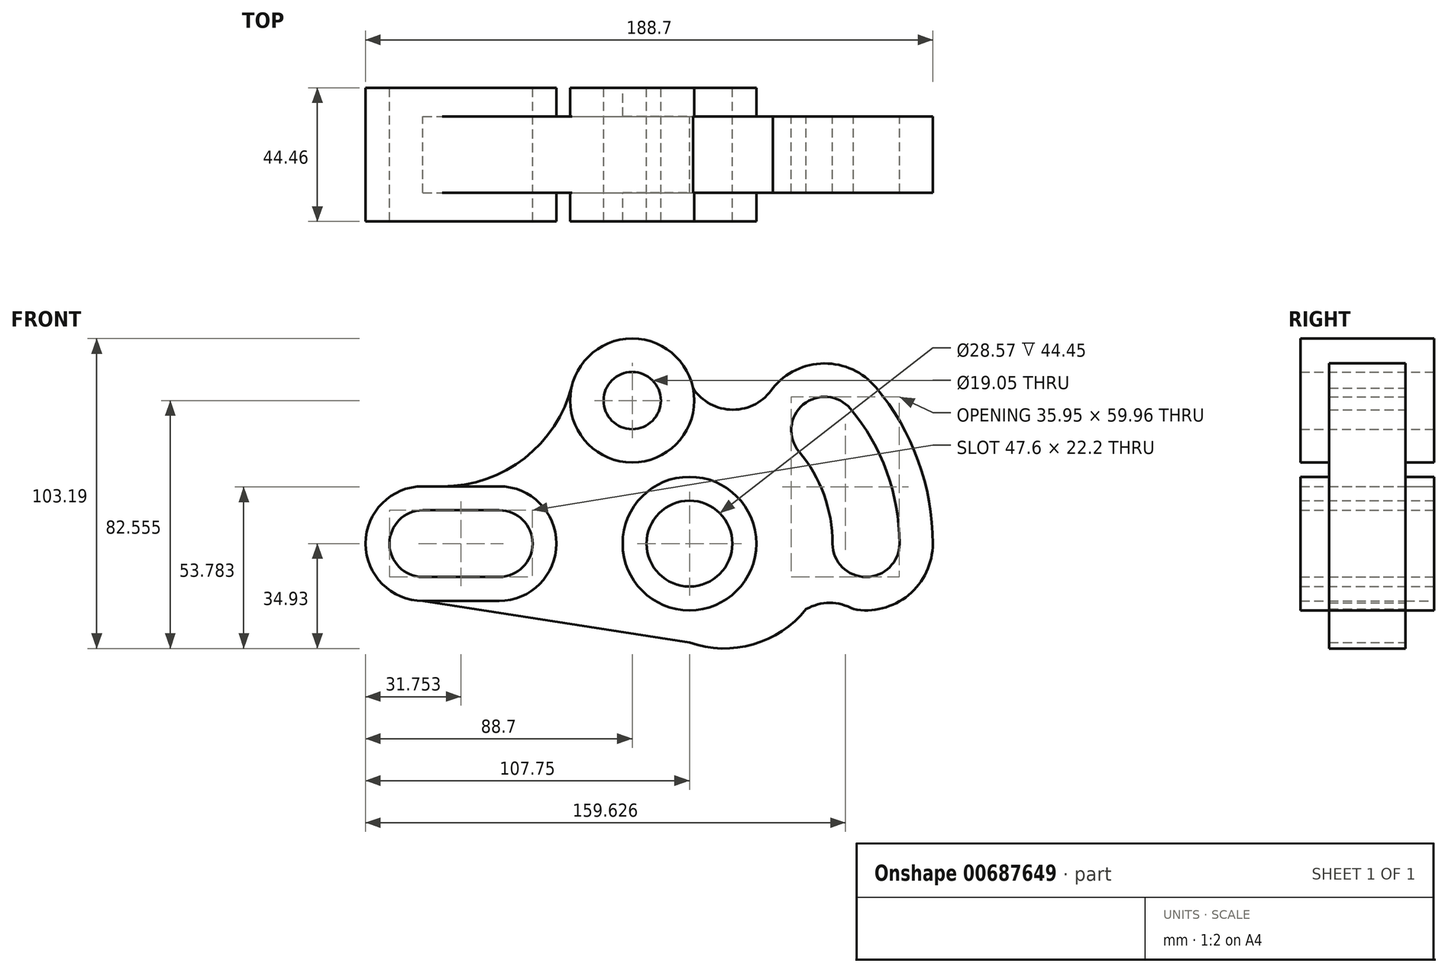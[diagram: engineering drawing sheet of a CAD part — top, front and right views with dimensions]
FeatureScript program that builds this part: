
annotation { "Feature Type Name" : "Feature", "Feature Type Description" : "" }
export const myFeature = defineFeature(function(context is Context, id is Id, definition is map)
    precondition{}
    {
        {
            var Q0;
            Q0=qCreatedBy(makeId("Front.planeOp"),FACE);
            var sketch = newSketch(context, id + "F0", { "sketchPlane" : qUnion([Q0])});
            skCircle(sketch, "E0", {"center": v(0, 0) * mm, "radius": 14.29 * mm});
            skCircle(sketch, "E1", {"center": v(0, 0) * mm, "radius": 22.23 * mm});
            skLineSegment(sketch, "E2", {"start": v(0, 0) * mm, "end": v(58.72, 0) * mm, "construction": true});
            skLineSegment(sketch, "E3", {"start": v(0, 0) * mm, "end": v(44.99, 37.75) * mm, "construction": true});
            skArc(sketch, "E4", {"start": v(44.99, 37.75) * mm, "mid": v(55.18, 20.09) * mm, "end": v(58.72, 0) * mm, "construction": true});
            skArc(sketch, "E5", {"start": v(36.46, 30.6) * mm, "mid": v(37.83, 46.27) * mm, "end": v(53.5, 44.9) * mm});
            skArc(sketch, "E6", {"start": v(47.6, 0) * mm, "mid": v(58.72, -11.13) * mm, "end": v(69.85, 0) * mm});
            skArc(sketch, "E7", {"start": v(53.5, 44.9) * mm, "mid": v(65.64, 23.9) * mm, "end": v(69.85, 0) * mm});
            skArc(sketch, "E8", {"start": v(36.46, 30.6) * mm, "mid": v(44.73, 16.28) * mm, "end": v(47.6, 0) * mm});
            skArc(sketch, "E9", {"start": v(-88.7, 11.1) * mm, "mid": v(-99.8, 0) * mm, "end": v(-88.7, -11.1) * mm});
            skArc(sketch, "E10", {"start": v(-63.3, 11.1) * mm, "mid": v(-52.2, 0) * mm, "end": v(-63.3, -11.1) * mm});
            skLineSegment(sketch, "E11", {"start": v(-88.7, 11.1) * mm, "end": v(-63.3, 11.1) * mm});
            skLineSegment(sketch, "E12", {"start": v(-88.7, -11.1) * mm, "end": v(-63.3, -11.1) * mm});
            skArc(sketch, "E13", {"start": v(-88.7, 19.05) * mm, "mid": v(-107.75, 0) * mm, "end": v(-88.7, -19.05) * mm});
            skLineSegment(sketch, "E14", {"start": v(-88.7, 19.05) * mm, "end": v(-63.3, 19.05) * mm});
            skLineSegment(sketch, "E15", {"start": v(-88.7, -19.05) * mm, "end": v(-63.3, -19.05) * mm});
            skArc(sketch, "E16", {"start": v(-63.3, -19.05) * mm, "mid": v(-44.25, 0) * mm, "end": v(-63.3, 19.05) * mm});
            skCircle(sketch, "E17", {"center": v(-19.05, 47.63) * mm, "radius": 9.53 * mm});
            skCircle(sketch, "E18", {"center": v(-19.05, 47.63) * mm, "radius": 20.64 * mm});
            skLineSegment(sketch, "E19", {"start": v(0, 0) * mm, "end": v(62.01, 52.03) * mm, "construction": true});
            skLineSegment(sketch, "E20", {"start": v(0, 0) * mm, "end": v(80.95, 0) * mm, "construction": true});
            skArc(sketch, "E21", {"start": v(27.74, 51.76) * mm, "mid": v(44.8, 59.97) * mm, "end": v(62.01, 52.03) * mm});
            skArc(sketch, "E22", {"start": v(62.01, 52.03) * mm, "mid": v(76.07, 27.69) * mm, "end": v(80.95, 0) * mm});
            skArc(sketch, "E23", {"start": v(80.95, 0) * mm, "mid": v(72.88, -17.14) * mm, "end": v(54.52, -21.82) * mm});
            skArc(sketch, "E24", {"start": v(58.72, 0) * mm, "mid": v(57.66, -11.11) * mm, "end": v(54.52, -21.82) * mm, "construction": true});
            skArc(sketch, "E25", {"start": v(44.99, 37.75) * mm, "mid": v(37.03, 45.58) * mm, "end": v(27.74, 51.76) * mm, "construction": true});
            skLineSegment(sketch, "E26", {"start": v(-88.7, -19.05) * mm, "end": v(0, -32.95) * mm});
            skArc(sketch, "E27", {"start": v(58.72, 0) * mm, "mid": v(55.63, -18.8) * mm, "end": v(46.68, -35.63) * mm, "construction": true});
            skArc(sketch, "E28", {"start": v(54.52, -21.82) * mm, "mid": v(46.68, -19.75) * mm, "end": v(38.84, -21.82) * mm});
            skArc(sketch, "E29", {"start": v(0, -32.95) * mm, "mid": v(21.2, -33.57) * mm, "end": v(38.84, -21.82) * mm});
            skArc(sketch, "E30", {"start": v(1.17, 51.76) * mm, "mid": v(14.45, 44.58) * mm, "end": v(27.74, 51.76) * mm});
            skArc(sketch, "E31", {"start": v(-82.17, 19.05) * mm, "mid": v(-54.84, 28.45) * mm, "end": v(-39.06, 52.66) * mm});
            skSolve(sketch);
        }
        {
            var Q0;
            Q0=makeQuery(id+"F0.imprint","IMPRINT",FACE,{"disambiguationData":[TD([[makeQuery(id+"F0.imprint","IMPRINT",EDGE,{"derivedFrom":sQuery(id+"F0.wireOp",EDGE,"E1")}),-1.0]])]});
            extrude(context, id + "F1", {"entities" : qUnion([Q0]), "endBound" : BoundingType.SYMMETRIC, "depth" : 25.4 * mm, "offsetDistance" : 25.4 * mm});
        }
        {
            var Q0;
            Q0=makeQuery(id+"F0.imprint","IMPRINT",FACE,{"disambiguationData":[TD([[makeQuery(id+"F0.imprint","IMPRINT",EDGE,{"derivedFrom":sQuery(id+"F0.wireOp",EDGE,"E9")}),-1.0]])]});
            var Q1;
            Q1=makeQuery(id+"F0.imprint","IMPRINT",FACE,{"disambiguationData":[TD([[makeQuery(id+"F0.imprint","IMPRINT",EDGE,{"derivedFrom":sQuery(id+"F0.wireOp",EDGE,"E17")}),-1.0]])]});
            var Q2;
            Q2=makeQuery(id+"F0.imprint","IMPRINT",FACE,{"disambiguationData":[TD([[makeQuery(id+"F0.imprint","IMPRINT",EDGE,{"derivedFrom":sQuery(id+"F0.wireOp",EDGE,"E0")}),-1.0]])]});
            extrude(context, id + "F2", {"entities" : qUnion([Q0, Q1, Q2]), "operationType" : NewBodyOperationType.ADD, "endBound" : BoundingType.SYMMETRIC, "depth" : 44.45 * mm, "offsetDistance" : 25.4 * mm});
        }
    });
